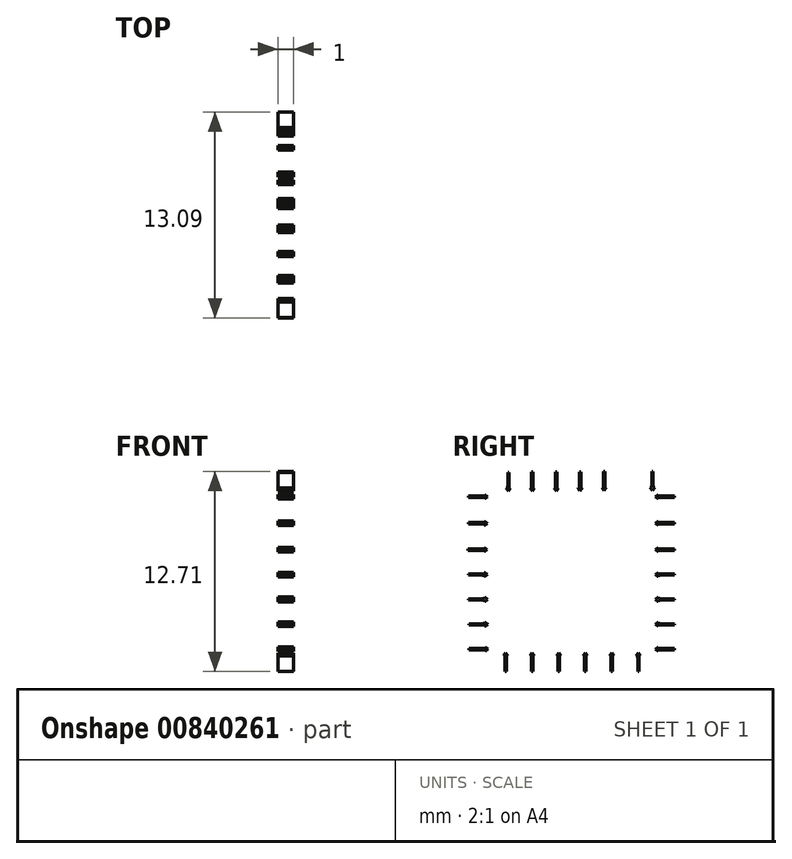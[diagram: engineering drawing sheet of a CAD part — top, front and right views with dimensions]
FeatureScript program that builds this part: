
annotation { "Feature Type Name" : "Feature", "Feature Type Description" : "" }
export const myFeature = defineFeature(function(context is Context, id is Id, definition is map)
    precondition{}
    {
        {
            var Q0;
            Q0=qCreatedBy(makeId("Right.planeOp"),FACE);
            var sketch = newSketch(context, id + "F0", { "sketchPlane" : qUnion([Q0])});
            skLineSegment(sketch, "E0.2.0", {"start": v(11.3, -4.37) * mm, "end": v(12.3, -4.37) * mm});
            skLineSegment(sketch, "E0.2.1", {"start": v(11.3, -4.55) * mm, "end": v(11.1, -4.4) * mm});
            skLineSegment(sketch, "E0.2.2", {"start": v(11.3, -4.44) * mm, "end": v(12.3, -4.44) * mm});
            skLineSegment(sketch, "E0.2.4", {"start": v(11.3, -4.26) * mm, "end": v(11.1, -4.4) * mm});
            skLineSegment(sketch, "E0.2.5", {"start": v(11.3, -4.44) * mm, "end": v(11.3, -4.55) * mm});
            skLineSegment(sketch, "E0.2.6", {"start": v(12.3, -4.44) * mm, "end": v(12.3, -4.37) * mm});
            skLineSegment(sketch, "E0.2.7", {"start": v(11.3, -4.37) * mm, "end": v(11.3, -4.26) * mm});
            skLineSegment(sketch, "E0.2.8", {"start": v(11.3, -4.44) * mm, "end": v(11.3, -4.37) * mm});
            skLineSegment(sketch, "E1.3.6.0", {"start": v(0.22, -4.26) * mm, "end": v(0.42, -4.4) * mm});
            skLineSegment(sketch, "E1.6.6.0", {"start": v(0.22, -4.37) * mm, "end": v(-0.78, -4.37) * mm});
            skLineSegment(sketch, "E1.8.6.0", {"start": v(0.22, -4.44) * mm, "end": v(-0.78, -4.44) * mm});
            skLineSegment(sketch, "E1.10.6.0", {"start": v(0.22, -4.55) * mm, "end": v(0.42, -4.4) * mm});
            skLineSegment(sketch, "E1.13.6.0", {"start": v(0.22, -4.37) * mm, "end": v(0.22, -4.26) * mm});
            skLineSegment(sketch, "E1.16.6.0", {"start": v(-0.78, -4.37) * mm, "end": v(-0.78, -4.44) * mm});
            skLineSegment(sketch, "E1.19.6.0", {"start": v(0.22, -4.44) * mm, "end": v(0.22, -4.55) * mm});
            skLineSegment(sketch, "E1.22.6.0", {"start": v(0.22, -4.37) * mm, "end": v(0.22, -4.44) * mm});
            skLineSegment(sketch, "E2.0.1.0", {"start": v(0.23, -2.76) * mm, "end": v(0.23, -2.87) * mm});
            skLineSegment(sketch, "E2.0.1.1", {"start": v(0.23, -2.58) * mm, "end": v(0.43, -2.72) * mm});
            skLineSegment(sketch, "E2.0.1.2", {"start": v(-0.77, -2.69) * mm, "end": v(-0.77, -2.76) * mm});
            skLineSegment(sketch, "E2.0.1.3", {"start": v(0.23, -2.87) * mm, "end": v(0.43, -2.72) * mm});
            skLineSegment(sketch, "E2.0.1.4", {"start": v(0.23, -2.69) * mm, "end": v(0.23, -2.58) * mm});
            skLineSegment(sketch, "E2.0.1.5", {"start": v(0.23, -2.69) * mm, "end": v(-0.77, -2.69) * mm});
            skLineSegment(sketch, "E2.0.1.6", {"start": v(0.23, -2.69) * mm, "end": v(0.23, -2.76) * mm});
            skLineSegment(sketch, "E2.0.1.7", {"start": v(0.23, -2.76) * mm, "end": v(-0.77, -2.76) * mm});
            skLineSegment(sketch, "E2.0.2.0", {"start": v(0.25, -1.08) * mm, "end": v(0.25, -1.2) * mm});
            skLineSegment(sketch, "E2.0.2.1", {"start": v(0.25, -0.9) * mm, "end": v(0.45, -1.04) * mm});
            skLineSegment(sketch, "E2.0.2.2", {"start": v(-0.76, -1) * mm, "end": v(-0.76, -1.08) * mm});
            skLineSegment(sketch, "E2.0.2.3", {"start": v(0.25, -1.2) * mm, "end": v(0.45, -1.04) * mm});
            skLineSegment(sketch, "E2.0.2.4", {"start": v(0.25, -1) * mm, "end": v(0.25, -0.9) * mm});
            skLineSegment(sketch, "E2.0.2.5", {"start": v(0.25, -1) * mm, "end": v(-0.76, -1) * mm});
            skLineSegment(sketch, "E2.0.2.6", {"start": v(0.25, -1) * mm, "end": v(0.25, -1.08) * mm});
            skLineSegment(sketch, "E2.0.2.7", {"start": v(0.25, -1.08) * mm, "end": v(-0.76, -1.08) * mm});
            skLineSegment(sketch, "E2.direction2", {"start": v(-0.78, -4.44) * mm, "end": v(-0.77, -2.76) * mm, "construction": true});
            skLineSegment(sketch, "E3.0.1.0", {"start": v(0.23, -6.13) * mm, "end": v(0.43, -5.98) * mm});
            skLineSegment(sketch, "E3.0.1.1", {"start": v(0.23, -6.02) * mm, "end": v(-0.77, -6.02) * mm});
            skLineSegment(sketch, "E3.0.1.2", {"start": v(0.23, -5.95) * mm, "end": v(-0.77, -5.95) * mm});
            skLineSegment(sketch, "E3.0.1.3", {"start": v(0.23, -6.02) * mm, "end": v(0.23, -6.13) * mm});
            skLineSegment(sketch, "E3.0.1.4", {"start": v(0.23, -5.84) * mm, "end": v(0.43, -5.98) * mm});
            skLineSegment(sketch, "E3.0.1.5", {"start": v(0.23, -5.95) * mm, "end": v(0.23, -5.84) * mm});
            skLineSegment(sketch, "E3.0.1.6", {"start": v(-0.77, -5.95) * mm, "end": v(-0.77, -6.02) * mm});
            skLineSegment(sketch, "E3.0.1.7", {"start": v(0.23, -5.95) * mm, "end": v(0.23, -6.02) * mm});
            skLineSegment(sketch, "E3.0.2.0", {"start": v(0.25, -7.71) * mm, "end": v(0.45, -7.56) * mm});
            skLineSegment(sketch, "E3.0.2.1", {"start": v(0.25, -7.6) * mm, "end": v(-0.76, -7.6) * mm});
            skLineSegment(sketch, "E3.0.2.2", {"start": v(0.25, -7.53) * mm, "end": v(-0.76, -7.53) * mm});
            skLineSegment(sketch, "E3.0.2.3", {"start": v(0.25, -7.6) * mm, "end": v(0.25, -7.71) * mm});
            skLineSegment(sketch, "E3.0.2.4", {"start": v(0.25, -7.42) * mm, "end": v(0.45, -7.56) * mm});
            skLineSegment(sketch, "E3.0.2.5", {"start": v(0.25, -7.53) * mm, "end": v(0.25, -7.42) * mm});
            skLineSegment(sketch, "E3.0.2.6", {"start": v(-0.76, -7.53) * mm, "end": v(-0.76, -7.6) * mm});
            skLineSegment(sketch, "E3.0.2.7", {"start": v(0.25, -7.53) * mm, "end": v(0.25, -7.6) * mm});
            skLineSegment(sketch, "E3.0.3.0", {"start": v(0.26, -9.29) * mm, "end": v(0.46, -9.14) * mm});
            skLineSegment(sketch, "E3.0.3.1", {"start": v(0.26, -9.18) * mm, "end": v(-0.75, -9.18) * mm});
            skLineSegment(sketch, "E3.0.3.2", {"start": v(0.26, -9.1) * mm, "end": v(-0.75, -9.1) * mm});
            skLineSegment(sketch, "E3.0.3.3", {"start": v(0.26, -9.18) * mm, "end": v(0.26, -9.29) * mm});
            skLineSegment(sketch, "E3.0.3.4", {"start": v(0.26, -9) * mm, "end": v(0.46, -9.14) * mm});
            skLineSegment(sketch, "E3.0.3.5", {"start": v(0.26, -9.1) * mm, "end": v(0.26, -9) * mm});
            skLineSegment(sketch, "E3.0.3.6", {"start": v(-0.75, -9.1) * mm, "end": v(-0.75, -9.18) * mm});
            skLineSegment(sketch, "E3.0.3.7", {"start": v(0.26, -9.1) * mm, "end": v(0.26, -9.18) * mm});
            skLineSegment(sketch, "E3.0.4.0", {"start": v(0.27, -10.87) * mm, "end": v(0.47, -10.72) * mm});
            skLineSegment(sketch, "E3.0.4.1", {"start": v(0.27, -10.76) * mm, "end": v(-0.73, -10.76) * mm});
            skLineSegment(sketch, "E3.0.4.2", {"start": v(0.27, -10.69) * mm, "end": v(-0.73, -10.69) * mm});
            skLineSegment(sketch, "E3.0.4.3", {"start": v(0.27, -10.76) * mm, "end": v(0.27, -10.87) * mm});
            skLineSegment(sketch, "E3.0.4.4", {"start": v(0.27, -10.57) * mm, "end": v(0.47, -10.72) * mm});
            skLineSegment(sketch, "E3.0.4.5", {"start": v(0.27, -10.69) * mm, "end": v(0.27, -10.57) * mm});
            skLineSegment(sketch, "E3.0.4.6", {"start": v(-0.73, -10.69) * mm, "end": v(-0.73, -10.76) * mm});
            skLineSegment(sketch, "E3.0.4.7", {"start": v(0.27, -10.69) * mm, "end": v(0.27, -10.76) * mm});
            skLineSegment(sketch, "E3.direction2", {"start": v(-0.78, -4.44) * mm, "end": v(-0.77, -6.02) * mm, "construction": true});
            skLineSegment(sketch, "E4.0.1.0", {"start": v(11.3, -2.58) * mm, "end": v(11.1, -2.72) * mm});
            skLineSegment(sketch, "E4.0.1.1", {"start": v(11.3, -2.76) * mm, "end": v(12.3, -2.76) * mm});
            skLineSegment(sketch, "E4.0.1.2", {"start": v(11.3, -2.87) * mm, "end": v(11.1, -2.72) * mm});
            skLineSegment(sketch, "E4.0.1.3", {"start": v(11.3, -2.69) * mm, "end": v(12.3, -2.69) * mm});
            skLineSegment(sketch, "E4.0.1.4", {"start": v(12.3, -2.76) * mm, "end": v(12.3, -2.69) * mm});
            skLineSegment(sketch, "E4.0.1.5", {"start": v(11.3, -2.76) * mm, "end": v(11.3, -2.87) * mm});
            skLineSegment(sketch, "E4.0.1.6", {"start": v(11.3, -2.69) * mm, "end": v(11.3, -2.58) * mm});
            skLineSegment(sketch, "E4.0.1.7", {"start": v(11.3, -2.76) * mm, "end": v(11.3, -2.69) * mm});
            skLineSegment(sketch, "E4.0.2.0", {"start": v(11.3, -0.9) * mm, "end": v(11.1, -1.04) * mm});
            skLineSegment(sketch, "E4.0.2.1", {"start": v(11.3, -1.08) * mm, "end": v(12.3, -1.08) * mm});
            skLineSegment(sketch, "E4.0.2.2", {"start": v(11.3, -1.19) * mm, "end": v(11.1, -1.04) * mm});
            skLineSegment(sketch, "E4.0.2.3", {"start": v(11.3, -1) * mm, "end": v(12.3, -1) * mm});
            skLineSegment(sketch, "E4.0.2.4", {"start": v(12.3, -1.08) * mm, "end": v(12.3, -1) * mm});
            skLineSegment(sketch, "E4.0.2.5", {"start": v(11.3, -1.08) * mm, "end": v(11.3, -1.19) * mm});
            skLineSegment(sketch, "E4.0.2.6", {"start": v(11.3, -1) * mm, "end": v(11.3, -0.9) * mm});
            skLineSegment(sketch, "E4.0.2.7", {"start": v(11.3, -1.08) * mm, "end": v(11.3, -1) * mm});
            skLineSegment(sketch, "E4.direction2", {"start": v(11.1, -4.4) * mm, "end": v(11.1, -2.72) * mm, "construction": true});
            skLineSegment(sketch, "E5.0", {"start": v(11.3, -5.95) * mm, "end": v(12.3, -5.95) * mm});
            skLineSegment(sketch, "E6.0.1.0", {"start": v(11.3, -6.02) * mm, "end": v(11.3, -5.95) * mm});
            skLineSegment(sketch, "E6.0.1.1", {"start": v(11.3, -6.02) * mm, "end": v(11.3, -6.13) * mm});
            skLineSegment(sketch, "E6.0.1.2", {"start": v(11.3, -6.02) * mm, "end": v(12.3, -6.02) * mm});
            skLineSegment(sketch, "E6.0.1.3", {"start": v(11.3, -5.84) * mm, "end": v(11.1, -5.98) * mm});
            skLineSegment(sketch, "E6.0.1.5", {"start": v(11.3, -5.95) * mm, "end": v(11.3, -5.84) * mm});
            skLineSegment(sketch, "E6.0.1.6", {"start": v(12.3, -6.02) * mm, "end": v(12.3, -5.95) * mm});
            skLineSegment(sketch, "E6.0.1.7", {"start": v(11.3, -6.13) * mm, "end": v(11.1, -5.98) * mm});
            skLineSegment(sketch, "E6.0.2.0", {"start": v(11.3, -7.6) * mm, "end": v(11.3, -7.53) * mm});
            skLineSegment(sketch, "E6.0.2.1", {"start": v(11.3, -7.6) * mm, "end": v(11.3, -7.71) * mm});
            skLineSegment(sketch, "E6.0.2.2", {"start": v(11.3, -7.6) * mm, "end": v(12.3, -7.6) * mm});
            skLineSegment(sketch, "E6.0.2.3", {"start": v(11.3, -7.42) * mm, "end": v(11.1, -7.56) * mm});
            skLineSegment(sketch, "E6.0.2.4", {"start": v(11.3, -7.53) * mm, "end": v(12.3, -7.53) * mm});
            skLineSegment(sketch, "E6.0.2.5", {"start": v(11.3, -7.53) * mm, "end": v(11.3, -7.42) * mm});
            skLineSegment(sketch, "E6.0.2.6", {"start": v(12.3, -7.6) * mm, "end": v(12.3, -7.53) * mm});
            skLineSegment(sketch, "E6.0.2.7", {"start": v(11.3, -7.71) * mm, "end": v(11.1, -7.56) * mm});
            skLineSegment(sketch, "E6.0.3.0", {"start": v(11.3, -9.18) * mm, "end": v(11.3, -9.1) * mm});
            skLineSegment(sketch, "E6.0.3.1", {"start": v(11.3, -9.18) * mm, "end": v(11.3, -9.3) * mm});
            skLineSegment(sketch, "E6.0.3.2", {"start": v(11.3, -9.18) * mm, "end": v(12.3, -9.18) * mm});
            skLineSegment(sketch, "E6.0.3.3", {"start": v(11.3, -9) * mm, "end": v(11.1, -9.14) * mm});
            skLineSegment(sketch, "E6.0.3.4", {"start": v(11.3, -9.1) * mm, "end": v(12.3, -9.1) * mm});
            skLineSegment(sketch, "E6.0.3.5", {"start": v(11.3, -9.1) * mm, "end": v(11.3, -9) * mm});
            skLineSegment(sketch, "E6.0.3.6", {"start": v(12.3, -9.18) * mm, "end": v(12.3, -9.1) * mm});
            skLineSegment(sketch, "E6.0.3.7", {"start": v(11.3, -9.3) * mm, "end": v(11.1, -9.14) * mm});
            skLineSegment(sketch, "E6.0.4.0", {"start": v(11.3, -10.76) * mm, "end": v(11.3, -10.69) * mm});
            skLineSegment(sketch, "E6.0.4.1", {"start": v(11.3, -10.76) * mm, "end": v(11.3, -10.87) * mm});
            skLineSegment(sketch, "E6.0.4.2", {"start": v(11.3, -10.76) * mm, "end": v(12.3, -10.76) * mm});
            skLineSegment(sketch, "E6.0.4.3", {"start": v(11.3, -10.58) * mm, "end": v(11.1, -10.72) * mm});
            skLineSegment(sketch, "E6.0.4.4", {"start": v(11.3, -10.69) * mm, "end": v(12.3, -10.69) * mm});
            skLineSegment(sketch, "E6.0.4.5", {"start": v(11.3, -10.69) * mm, "end": v(11.3, -10.58) * mm});
            skLineSegment(sketch, "E6.0.4.6", {"start": v(12.3, -10.76) * mm, "end": v(12.3, -10.69) * mm});
            skLineSegment(sketch, "E6.0.4.7", {"start": v(11.3, -10.87) * mm, "end": v(11.1, -10.72) * mm});
            skLineSegment(sketch, "E6.direction2", {"start": v(11.1, -4.4) * mm, "end": v(11.1, -5.98) * mm, "construction": true});
            skLineSegment(sketch, "E7", {"start": v(1.56, -11.15) * mm, "end": v(1.56, -12.15) * mm});
            skLineSegment(sketch, "E8", {"start": v(1.63, -11.15) * mm, "end": v(1.63, -12.15) * mm});
            skLineSegment(sketch, "E9", {"start": v(1.56, -12.15) * mm, "end": v(1.63, -12.15) * mm});
            skLineSegment(sketch, "E10", {"start": v(1.56, -11.15) * mm, "end": v(1.63, -11.15) * mm});
            skLineSegment(sketch, "E11", {"start": v(1.56, -11.15) * mm, "end": v(1.45, -11.15) * mm});
            skLineSegment(sketch, "E12", {"start": v(1.45, -11.15) * mm, "end": v(1.6, -10.95) * mm});
            skLineSegment(sketch, "E13", {"start": v(1.63, -11.15) * mm, "end": v(1.75, -11.15) * mm});
            skLineSegment(sketch, "E14", {"start": v(1.75, -11.15) * mm, "end": v(1.6, -10.95) * mm});
            skLineSegment(sketch, "E15.1.0.0", {"start": v(3.25, -11.15) * mm, "end": v(3.25, -12.15) * mm});
            skLineSegment(sketch, "E15.1.0.1", {"start": v(3.32, -11.15) * mm, "end": v(3.32, -12.15) * mm});
            skLineSegment(sketch, "E15.1.0.2", {"start": v(3.25, -12.15) * mm, "end": v(3.32, -12.15) * mm});
            skLineSegment(sketch, "E15.1.0.3", {"start": v(3.25, -11.15) * mm, "end": v(3.14, -11.15) * mm});
            skLineSegment(sketch, "E15.1.0.4", {"start": v(3.14, -11.15) * mm, "end": v(3.28, -10.95) * mm});
            skLineSegment(sketch, "E15.1.0.5", {"start": v(3.43, -11.15) * mm, "end": v(3.28, -10.95) * mm});
            skLineSegment(sketch, "E15.1.0.6", {"start": v(3.32, -11.15) * mm, "end": v(3.43, -11.15) * mm});
            skLineSegment(sketch, "E15.1.0.7", {"start": v(3.25, -11.15) * mm, "end": v(3.32, -11.15) * mm});
            skLineSegment(sketch, "E15.2.0.0", {"start": v(4.93, -11.15) * mm, "end": v(4.93, -12.15) * mm});
            skLineSegment(sketch, "E15.2.0.1", {"start": v(5, -11.15) * mm, "end": v(5, -12.15) * mm});
            skLineSegment(sketch, "E15.2.0.2", {"start": v(4.93, -12.15) * mm, "end": v(5, -12.15) * mm});
            skLineSegment(sketch, "E15.2.0.3", {"start": v(4.93, -11.15) * mm, "end": v(4.82, -11.15) * mm});
            skLineSegment(sketch, "E15.2.0.4", {"start": v(4.82, -11.15) * mm, "end": v(4.97, -10.95) * mm});
            skLineSegment(sketch, "E15.2.0.5", {"start": v(5.11, -11.15) * mm, "end": v(4.97, -10.95) * mm});
            skLineSegment(sketch, "E15.2.0.6", {"start": v(5, -11.15) * mm, "end": v(5.11, -11.15) * mm});
            skLineSegment(sketch, "E15.2.0.7", {"start": v(4.93, -11.15) * mm, "end": v(5, -11.15) * mm});
            skLineSegment(sketch, "E15.3.0.0", {"start": v(6.62, -11.15) * mm, "end": v(6.62, -12.15) * mm});
            skLineSegment(sketch, "E15.3.0.1", {"start": v(6.69, -11.15) * mm, "end": v(6.69, -12.15) * mm});
            skLineSegment(sketch, "E15.3.0.2", {"start": v(6.62, -12.15) * mm, "end": v(6.69, -12.15) * mm});
            skLineSegment(sketch, "E15.3.0.3", {"start": v(6.62, -11.15) * mm, "end": v(6.5, -11.15) * mm});
            skLineSegment(sketch, "E15.3.0.4", {"start": v(6.5, -11.15) * mm, "end": v(6.65, -10.95) * mm});
            skLineSegment(sketch, "E15.3.0.5", {"start": v(6.8, -11.15) * mm, "end": v(6.65, -10.95) * mm});
            skLineSegment(sketch, "E15.3.0.6", {"start": v(6.69, -11.15) * mm, "end": v(6.8, -11.15) * mm});
            skLineSegment(sketch, "E15.3.0.7", {"start": v(6.62, -11.15) * mm, "end": v(6.69, -11.15) * mm});
            skLineSegment(sketch, "E15.4.0.0", {"start": v(8.3, -11.15) * mm, "end": v(8.3, -12.15) * mm});
            skLineSegment(sketch, "E15.4.0.1", {"start": v(8.37, -11.15) * mm, "end": v(8.37, -12.15) * mm});
            skLineSegment(sketch, "E15.4.0.2", {"start": v(8.3, -12.15) * mm, "end": v(8.37, -12.15) * mm});
            skLineSegment(sketch, "E15.4.0.3", {"start": v(8.3, -11.15) * mm, "end": v(8.19, -11.15) * mm});
            skLineSegment(sketch, "E15.4.0.4", {"start": v(8.19, -11.15) * mm, "end": v(8.34, -10.95) * mm});
            skLineSegment(sketch, "E15.4.0.5", {"start": v(8.48, -11.15) * mm, "end": v(8.34, -10.95) * mm});
            skLineSegment(sketch, "E15.4.0.6", {"start": v(8.37, -11.15) * mm, "end": v(8.48, -11.15) * mm});
            skLineSegment(sketch, "E15.4.0.7", {"start": v(8.3, -11.15) * mm, "end": v(8.37, -11.15) * mm});
            skLineSegment(sketch, "E15.5.0.0", {"start": v(9.98, -11.15) * mm, "end": v(9.98, -12.15) * mm});
            skLineSegment(sketch, "E15.5.0.1", {"start": v(10.06, -11.15) * mm, "end": v(10.06, -12.15) * mm});
            skLineSegment(sketch, "E15.5.0.2", {"start": v(9.98, -12.15) * mm, "end": v(10.06, -12.15) * mm});
            skLineSegment(sketch, "E15.5.0.3", {"start": v(9.98, -11.15) * mm, "end": v(9.87, -11.15) * mm});
            skLineSegment(sketch, "E15.5.0.4", {"start": v(9.87, -11.15) * mm, "end": v(10.02, -10.95) * mm});
            skLineSegment(sketch, "E15.5.0.5", {"start": v(10.17, -11.15) * mm, "end": v(10.02, -10.95) * mm});
            skLineSegment(sketch, "E15.5.0.6", {"start": v(10.06, -11.15) * mm, "end": v(10.17, -11.15) * mm});
            skLineSegment(sketch, "E15.5.0.7", {"start": v(9.98, -11.15) * mm, "end": v(10.06, -11.15) * mm});
            skLineSegment(sketch, "E15.direction1", {"start": v(1.56, -12.15) * mm, "end": v(3.25, -12.15) * mm, "construction": true});
            skLineSegment(sketch, "E16.4.0", {"start": v(1.73, -0.49) * mm, "end": v(1.73, 0.52) * mm});
            skLineSegment(sketch, "E16.4.1", {"start": v(1.92, -0.49) * mm, "end": v(1.77, -0.69) * mm});
            skLineSegment(sketch, "E16.4.2", {"start": v(1.8, -0.49) * mm, "end": v(1.8, 0.52) * mm});
            skLineSegment(sketch, "E16.4.4", {"start": v(1.62, -0.49) * mm, "end": v(1.77, -0.69) * mm});
            skLineSegment(sketch, "E16.4.5", {"start": v(1.8, -0.49) * mm, "end": v(1.92, -0.49) * mm});
            skLineSegment(sketch, "E16.4.6", {"start": v(1.8, 0.52) * mm, "end": v(1.73, 0.52) * mm});
            skLineSegment(sketch, "E16.4.8", {"start": v(1.8, -0.49) * mm, "end": v(1.73, -0.49) * mm});
            skLineSegment(sketch, "E17.1.0.0", {"start": v(3.33, -0.48) * mm, "end": v(3.33, 0.52) * mm});
            skLineSegment(sketch, "E17.1.0.1", {"start": v(3.25, -0.48) * mm, "end": v(3.25, 0.52) * mm});
            skLineSegment(sketch, "E17.1.0.2", {"start": v(3.14, -0.48) * mm, "end": v(3.29, -0.68) * mm});
            skLineSegment(sketch, "E17.1.0.3", {"start": v(3.33, 0.52) * mm, "end": v(3.25, 0.52) * mm});
            skLineSegment(sketch, "E17.1.0.4", {"start": v(3.44, -0.48) * mm, "end": v(3.29, -0.68) * mm});
            skLineSegment(sketch, "E17.1.0.5", {"start": v(3.33, -0.48) * mm, "end": v(3.25, -0.48) * mm});
            skLineSegment(sketch, "E17.1.0.6", {"start": v(3.33, -0.48) * mm, "end": v(3.44, -0.48) * mm});
            skLineSegment(sketch, "E17.2.0.0", {"start": v(4.85, -0.47) * mm, "end": v(4.85, 0.53) * mm});
            skLineSegment(sketch, "E17.2.0.1", {"start": v(4.77, -0.47) * mm, "end": v(4.77, 0.53) * mm});
            skLineSegment(sketch, "E17.2.0.2", {"start": v(4.66, -0.47) * mm, "end": v(4.81, -0.67) * mm});
            skLineSegment(sketch, "E17.2.0.3", {"start": v(4.85, 0.53) * mm, "end": v(4.77, 0.53) * mm});
            skLineSegment(sketch, "E17.2.0.4", {"start": v(4.96, -0.47) * mm, "end": v(4.81, -0.67) * mm});
            skLineSegment(sketch, "E17.2.0.5", {"start": v(4.85, -0.47) * mm, "end": v(4.77, -0.47) * mm});
            skLineSegment(sketch, "E17.2.0.6", {"start": v(4.85, -0.47) * mm, "end": v(4.96, -0.47) * mm});
            skLineSegment(sketch, "E17.3.0.0", {"start": v(6.37, -0.46) * mm, "end": v(6.37, 0.54) * mm});
            skLineSegment(sketch, "E17.3.0.1", {"start": v(6.3, -0.46) * mm, "end": v(6.3, 0.54) * mm});
            skLineSegment(sketch, "E17.3.0.2", {"start": v(6.18, -0.46) * mm, "end": v(6.33, -0.66) * mm});
            skLineSegment(sketch, "E17.3.0.3", {"start": v(6.37, 0.54) * mm, "end": v(6.3, 0.54) * mm});
            skLineSegment(sketch, "E17.3.0.4", {"start": v(6.48, -0.46) * mm, "end": v(6.33, -0.66) * mm});
            skLineSegment(sketch, "E17.3.0.5", {"start": v(6.37, -0.46) * mm, "end": v(6.3, -0.46) * mm});
            skLineSegment(sketch, "E17.3.0.6", {"start": v(6.37, -0.46) * mm, "end": v(6.48, -0.46) * mm});
            skLineSegment(sketch, "E17.4.0.0", {"start": v(7.89, -0.45) * mm, "end": v(7.89, 0.55) * mm});
            skLineSegment(sketch, "E17.4.0.1", {"start": v(7.81, -0.45) * mm, "end": v(7.81, 0.55) * mm});
            skLineSegment(sketch, "E17.4.0.2", {"start": v(7.7, -0.45) * mm, "end": v(7.85, -0.65) * mm});
            skLineSegment(sketch, "E17.4.0.3", {"start": v(7.89, 0.55) * mm, "end": v(7.81, 0.55) * mm});
            skLineSegment(sketch, "E17.4.0.4", {"start": v(8, -0.45) * mm, "end": v(7.85, -0.65) * mm});
            skLineSegment(sketch, "E17.4.0.5", {"start": v(7.89, -0.45) * mm, "end": v(7.81, -0.45) * mm});
            skLineSegment(sketch, "E17.4.0.6", {"start": v(7.89, -0.45) * mm, "end": v(8, -0.45) * mm});
            skLineSegment(sketch, "E17.5.0.0", {"start": v(10.96, -0.44) * mm, "end": v(10.96, 0.56) * mm});
            skLineSegment(sketch, "E17.5.0.1", {"start": v(10.89, -0.44) * mm, "end": v(10.89, 0.56) * mm});
            skLineSegment(sketch, "E17.5.0.2", {"start": v(10.78, -0.44) * mm, "end": v(10.92, -0.64) * mm});
            skLineSegment(sketch, "E17.5.0.3", {"start": v(10.96, 0.56) * mm, "end": v(10.89, 0.56) * mm});
            skLineSegment(sketch, "E17.5.0.4", {"start": v(11.07, -0.44) * mm, "end": v(10.92, -0.64) * mm});
            skLineSegment(sketch, "E17.5.0.5", {"start": v(10.96, -0.44) * mm, "end": v(10.89, -0.44) * mm});
            skLineSegment(sketch, "E17.5.0.6", {"start": v(10.96, -0.44) * mm, "end": v(11.07, -0.44) * mm});
            skLineSegment(sketch, "E17.direction1", {"start": v(1.77, -0.69) * mm, "end": v(3.29, -0.68) * mm, "construction": true});
            skLineSegment(sketch, "E18", {"start": v(1.73, -0.49) * mm, "end": v(1.62, -0.49) * mm});
            skLineSegment(sketch, "E19", {"start": v(3.14, -0.48) * mm, "end": v(3.25, -0.48) * mm});
            skLineSegment(sketch, "E20", {"start": v(4.77, -0.47) * mm, "end": v(4.66, -0.47) * mm});
            skLineSegment(sketch, "E21", {"start": v(6.3, -0.46) * mm, "end": v(6.18, -0.46) * mm});
            skLineSegment(sketch, "E22", {"start": v(7.81, -0.45) * mm, "end": v(7.7, -0.45) * mm});
            skLineSegment(sketch, "E23", {"start": v(10.89, -0.44) * mm, "end": v(10.78, -0.44) * mm});
            skSolve(sketch);
        }
        {
            var Q0;
            Q0=makeQuery(id+"F0.imprint","IMPRINT",FACE,{"disambiguationData":[TD([[makeQuery(id+"F0.imprint","IMPRINT",EDGE,{"derivedFrom":sQuery(id+"F0.wireOp",EDGE,"E4.0.1.1")}),1.0]])]});
            var Q1;
            Q1=makeQuery(id+"F0.imprint","IMPRINT",FACE,{"disambiguationData":[TD([[makeQuery(id+"F0.imprint","IMPRINT",EDGE,{"derivedFrom":sQuery(id+"F0.wireOp",EDGE,"E0.2.0")}),-1.0]])]});
            var Q2;
            Q2=makeQuery(id+"F0.imprint","IMPRINT",FACE,{"disambiguationData":[TD([[makeQuery(id+"F0.imprint","IMPRINT",EDGE,{"derivedFrom":sQuery(id+"F0.wireOp",EDGE,"E3.0.3.1")}),-1.0]])]});
            var Q3;
            Q3=makeQuery(id+"F0.imprint","IMPRINT",FACE,{"disambiguationData":[TD([[makeQuery(id+"F0.imprint","IMPRINT",EDGE,{"derivedFrom":sQuery(id+"F0.wireOp",EDGE,"E6.0.2.0")}),-1.0]])]});
            var Q4;
            Q4=makeQuery(id+"F0.imprint","IMPRINT",FACE,{"disambiguationData":[TD([[makeQuery(id+"F0.imprint","IMPRINT",EDGE,{"derivedFrom":sQuery(id+"F0.wireOp",EDGE,"E6.0.3.0")}),-1.0]])]});
            var Q5;
            Q5=makeQuery(id+"F0.imprint","IMPRINT",FACE,{"disambiguationData":[TD([[makeQuery(id+"F0.imprint","IMPRINT",EDGE,{"derivedFrom":sQuery(id+"F0.wireOp",EDGE,"E6.0.4.0")}),-1.0]])]});
            var Q6;
            Q6=makeQuery(id+"F0.imprint","IMPRINT",FACE,{"disambiguationData":[TD([[makeQuery(id+"F0.imprint","IMPRINT",EDGE,{"derivedFrom":sQuery(id+"F0.wireOp",EDGE,"E4.0.2.1")}),1.0]])]});
            var Q7;
            Q7=makeQuery(id+"F0.imprint","IMPRINT",FACE,{"disambiguationData":[TD([[makeQuery(id+"F0.imprint","IMPRINT",EDGE,{"derivedFrom":sQuery(id+"F0.wireOp",EDGE,"E3.0.4.1")}),-1.0]])]});
            var Q8;
            Q8=makeQuery(id+"F0.imprint","IMPRINT",FACE,{"disambiguationData":[TD([[makeQuery(id+"F0.imprint","IMPRINT",EDGE,{"derivedFrom":sQuery(id+"F0.wireOp",EDGE,"E6.0.1.0")}),-1.0]])]});
            var Q9;
            Q9=makeQuery(id+"F0.imprint","IMPRINT",FACE,{"disambiguationData":[TD([[makeQuery(id+"F0.imprint","IMPRINT",EDGE,{"derivedFrom":sQuery(id+"F0.wireOp",EDGE,"E17.2.0.0")}),1.0]])]});
            var Q10;
            Q10=makeQuery(id+"F0.imprint","IMPRINT",FACE,{"disambiguationData":[TD([[makeQuery(id+"F0.imprint","IMPRINT",EDGE,{"derivedFrom":sQuery(id+"F0.wireOp",EDGE,"E17.5.0.0")}),1.0]])]});
            var Q11;
            Q11=makeQuery(id+"F0.imprint","IMPRINT",FACE,{"disambiguationData":[TD([[makeQuery(id+"F0.imprint","IMPRINT",EDGE,{"derivedFrom":sQuery(id+"F0.wireOp",EDGE,"E15.5.0.0")}),1.0]])]});
            var Q12;
            Q12=makeQuery(id+"F0.imprint","IMPRINT",FACE,{"disambiguationData":[TD([[makeQuery(id+"F0.imprint","IMPRINT",EDGE,{"derivedFrom":sQuery(id+"F0.wireOp",EDGE,"E3.0.1.1")}),-1.0]])]});
            var Q13;
            Q13=makeQuery(id+"F0.imprint","IMPRINT",FACE,{"disambiguationData":[TD([[makeQuery(id+"F0.imprint","IMPRINT",EDGE,{"derivedFrom":sQuery(id+"F0.wireOp",EDGE,"E15.4.0.0")}),1.0]])]});
            var Q14;
            Q14=makeQuery(id+"F0.imprint","IMPRINT",FACE,{"disambiguationData":[TD([[makeQuery(id+"F0.imprint","IMPRINT",EDGE,{"derivedFrom":sQuery(id+"F0.wireOp",EDGE,"E17.1.0.0")}),1.0]])]});
            var Q15;
            Q15=makeQuery(id+"F0.imprint","IMPRINT",FACE,{"disambiguationData":[TD([[makeQuery(id+"F0.imprint","IMPRINT",EDGE,{"derivedFrom":sQuery(id+"F0.wireOp",EDGE,"E7")}),1.0]])]});
            var Q16;
            Q16=makeQuery(id+"F0.imprint","IMPRINT",FACE,{"disambiguationData":[TD([[makeQuery(id+"F0.imprint","IMPRINT",EDGE,{"derivedFrom":sQuery(id+"F0.wireOp",EDGE,"E17.4.0.0")}),1.0]])]});
            var Q17;
            Q17=makeQuery(id+"F0.imprint","IMPRINT",FACE,{"disambiguationData":[TD([[makeQuery(id+"F0.imprint","IMPRINT",EDGE,{"derivedFrom":sQuery(id+"F0.wireOp",EDGE,"E16.4.0")}),-1.0]])]});
            var Q18;
            Q18=makeQuery(id+"F0.imprint","IMPRINT",FACE,{"disambiguationData":[TD([[makeQuery(id+"F0.imprint","IMPRINT",EDGE,{"derivedFrom":sQuery(id+"F0.wireOp",EDGE,"E2.0.2.2")}),1.0]])]});
            var Q19;
            Q19=makeQuery(id+"F0.imprint","IMPRINT",FACE,{"disambiguationData":[TD([[makeQuery(id+"F0.imprint","IMPRINT",EDGE,{"derivedFrom":sQuery(id+"F0.wireOp",EDGE,"E17.3.0.0")}),1.0]])]});
            var Q20;
            Q20=makeQuery(id+"F0.imprint","IMPRINT",FACE,{"disambiguationData":[TD([[makeQuery(id+"F0.imprint","IMPRINT",EDGE,{"derivedFrom":sQuery(id+"F0.wireOp",EDGE,"E15.3.0.0")}),1.0]])]});
            var Q21;
            Q21=makeQuery(id+"F0.imprint","IMPRINT",FACE,{"disambiguationData":[TD([[makeQuery(id+"F0.imprint","IMPRINT",EDGE,{"derivedFrom":sQuery(id+"F0.wireOp",EDGE,"E17.2.0.2")}),1.0]])]});
            var Q22;
            Q22=makeQuery(id+"F0.imprint","IMPRINT",FACE,{"disambiguationData":[TD([[makeQuery(id+"F0.imprint","IMPRINT",EDGE,{"derivedFrom":sQuery(id+"F0.wireOp",EDGE,"E15.2.0.0")}),1.0]])]});
            var Q23;
            Q23=makeQuery(id+"F0.imprint","IMPRINT",FACE,{"disambiguationData":[TD([[makeQuery(id+"F0.imprint","IMPRINT",EDGE,{"derivedFrom":sQuery(id+"F0.wireOp",EDGE,"E3.0.1.0")}),1.0]])]});
            var Q24;
            Q24=makeQuery(id+"F0.imprint","IMPRINT",FACE,{"disambiguationData":[TD([[makeQuery(id+"F0.imprint","IMPRINT",EDGE,{"derivedFrom":sQuery(id+"F0.wireOp",EDGE,"E0.2.1")}),-1.0]])]});
            var Q25;
            Q25=makeQuery(id+"F0.imprint","IMPRINT",FACE,{"disambiguationData":[TD([[makeQuery(id+"F0.imprint","IMPRINT",EDGE,{"derivedFrom":sQuery(id+"F0.wireOp",EDGE,"E10")}),1.0]])]});
            var Q26;
            Q26=makeQuery(id+"F0.imprint","IMPRINT",FACE,{"disambiguationData":[TD([[makeQuery(id+"F0.imprint","IMPRINT",EDGE,{"derivedFrom":sQuery(id+"F0.wireOp",EDGE,"E2.0.1.2")}),1.0]])]});
            var Q27;
            Q27=makeQuery(id+"F0.imprint","IMPRINT",FACE,{"disambiguationData":[TD([[makeQuery(id+"F0.imprint","IMPRINT",EDGE,{"derivedFrom":sQuery(id+"F0.wireOp",EDGE,"E3.0.2.1")}),-1.0]])]});
            var Q28;
            Q28=makeQuery(id+"F0.imprint","IMPRINT",FACE,{"disambiguationData":[TD([[makeQuery(id+"F0.imprint","IMPRINT",EDGE,{"derivedFrom":sQuery(id+"F0.wireOp",EDGE,"E15.1.0.0")}),1.0]])]});
            var Q29;
            Q29=makeQuery(id+"F0.imprint","IMPRINT",FACE,{"disambiguationData":[TD([[makeQuery(id+"F0.imprint","IMPRINT",EDGE,{"derivedFrom":sQuery(id+"F0.wireOp",EDGE,"E1.6.6.0")}),1.0]])]});
            var Q30;
            Q30=makeQuery(id+"F0.imprint","IMPRINT",FACE,{"disambiguationData":[TD([[makeQuery(id+"F0.imprint","IMPRINT",EDGE,{"derivedFrom":sQuery(id+"F0.wireOp",EDGE,"E4.0.1.0")}),1.0]])]});
            var Q31;
            Q31=makeQuery(id+"F0.imprint","IMPRINT",FACE,{"disambiguationData":[TD([[makeQuery(id+"F0.imprint","IMPRINT",EDGE,{"derivedFrom":sQuery(id+"F0.wireOp",EDGE,"E1.3.6.0")}),-1.0]])]});
            var Q32;
            Q32=makeQuery(id+"F0.imprint","IMPRINT",FACE,{"disambiguationData":[TD([[makeQuery(id+"F0.imprint","IMPRINT",EDGE,{"derivedFrom":sQuery(id+"F0.wireOp",EDGE,"E17.1.0.2")}),1.0]])]});
            var Q33;
            Q33=makeQuery(id+"F0.imprint","IMPRINT",FACE,{"disambiguationData":[TD([[makeQuery(id+"F0.imprint","IMPRINT",EDGE,{"derivedFrom":sQuery(id+"F0.wireOp",EDGE,"E17.5.0.2")}),1.0]])]});
            var Q34;
            Q34=makeQuery(id+"F0.imprint","IMPRINT",FACE,{"disambiguationData":[TD([[makeQuery(id+"F0.imprint","IMPRINT",EDGE,{"derivedFrom":sQuery(id+"F0.wireOp",EDGE,"E15.4.0.3")}),-1.0]])]});
            var Q35;
            Q35=makeQuery(id+"F0.imprint","IMPRINT",FACE,{"disambiguationData":[TD([[makeQuery(id+"F0.imprint","IMPRINT",EDGE,{"derivedFrom":sQuery(id+"F0.wireOp",EDGE,"E15.5.0.3")}),-1.0]])]});
            var Q36;
            Q36=makeQuery(id+"F0.imprint","IMPRINT",FACE,{"disambiguationData":[TD([[makeQuery(id+"F0.imprint","IMPRINT",EDGE,{"derivedFrom":sQuery(id+"F0.wireOp",EDGE,"E15.1.0.3")}),-1.0]])]});
            var Q37;
            Q37=makeQuery(id+"F0.imprint","IMPRINT",FACE,{"disambiguationData":[TD([[makeQuery(id+"F0.imprint","IMPRINT",EDGE,{"derivedFrom":sQuery(id+"F0.wireOp",EDGE,"E2.0.1.0")}),1.0]])]});
            var Q38;
            Q38=makeQuery(id+"F0.imprint","IMPRINT",FACE,{"disambiguationData":[TD([[makeQuery(id+"F0.imprint","IMPRINT",EDGE,{"derivedFrom":sQuery(id+"F0.wireOp",EDGE,"E17.4.0.2")}),1.0]])]});
            var Q39;
            {var subQ3=sQuery(id+"F0.wireOp",EDGE,"E6.0.1.0");Q39=makeQuery(id+"F0.imprint","IMPRINT",FACE,{"disambiguationData":[TD([[makeQuery(id+"F0.imprint","IMPRINT",EDGE,{"derivedFrom":subQ3}),1.0]])]});}
            var Q40;
            Q40=makeQuery(id+"F0.imprint","IMPRINT",FACE,{"disambiguationData":[TD([[makeQuery(id+"F0.imprint","IMPRINT",EDGE,{"derivedFrom":sQuery(id+"F0.wireOp",EDGE,"E3.0.2.0")}),1.0]])]});
            var Q41;
            Q41=makeQuery(id+"F0.imprint","IMPRINT",FACE,{"disambiguationData":[TD([[makeQuery(id+"F0.imprint","IMPRINT",EDGE,{"derivedFrom":sQuery(id+"F0.wireOp",EDGE,"E2.0.2.0")}),1.0]])]});
            var Q42;
            Q42=makeQuery(id+"F0.imprint","IMPRINT",FACE,{"disambiguationData":[TD([[makeQuery(id+"F0.imprint","IMPRINT",EDGE,{"derivedFrom":sQuery(id+"F0.wireOp",EDGE,"E15.3.0.3")}),-1.0]])]});
            var Q43;
            Q43=makeQuery(id+"F0.imprint","IMPRINT",FACE,{"disambiguationData":[TD([[makeQuery(id+"F0.imprint","IMPRINT",EDGE,{"derivedFrom":sQuery(id+"F0.wireOp",EDGE,"E15.2.0.3")}),-1.0]])]});
            var Q44;
            Q44=makeQuery(id+"F0.imprint","IMPRINT",FACE,{"disambiguationData":[TD([[makeQuery(id+"F0.imprint","IMPRINT",EDGE,{"derivedFrom":sQuery(id+"F0.wireOp",EDGE,"E6.0.2.0")}),1.0]])]});
            var Q45;
            Q45=makeQuery(id+"F0.imprint","IMPRINT",FACE,{"disambiguationData":[TD([[makeQuery(id+"F0.imprint","IMPRINT",EDGE,{"derivedFrom":sQuery(id+"F0.wireOp",EDGE,"E6.0.4.0")}),1.0]])]});
            var Q46;
            Q46=makeQuery(id+"F0.imprint","IMPRINT",FACE,{"disambiguationData":[TD([[makeQuery(id+"F0.imprint","IMPRINT",EDGE,{"derivedFrom":sQuery(id+"F0.wireOp",EDGE,"E17.3.0.2")}),1.0]])]});
            var Q47;
            Q47=makeQuery(id+"F0.imprint","IMPRINT",FACE,{"disambiguationData":[TD([[makeQuery(id+"F0.imprint","IMPRINT",EDGE,{"derivedFrom":sQuery(id+"F0.wireOp",EDGE,"E16.4.1")}),-1.0]])]});
            var Q48;
            Q48=makeQuery(id+"F0.imprint","IMPRINT",FACE,{"disambiguationData":[TD([[makeQuery(id+"F0.imprint","IMPRINT",EDGE,{"derivedFrom":sQuery(id+"F0.wireOp",EDGE,"E6.0.3.0")}),1.0]])]});
            var Q49;
            Q49=makeQuery(id+"F0.imprint","IMPRINT",FACE,{"disambiguationData":[TD([[makeQuery(id+"F0.imprint","IMPRINT",EDGE,{"derivedFrom":sQuery(id+"F0.wireOp",EDGE,"E4.0.2.0")}),1.0]])]});
            var Q50;
            Q50=makeQuery(id+"F0.imprint","IMPRINT",FACE,{"disambiguationData":[TD([[makeQuery(id+"F0.imprint","IMPRINT",EDGE,{"derivedFrom":sQuery(id+"F0.wireOp",EDGE,"E3.0.3.0")}),1.0]])]});
            var Q51;
            Q51=makeQuery(id+"F0.imprint","IMPRINT",FACE,{"disambiguationData":[TD([[makeQuery(id+"F0.imprint","IMPRINT",EDGE,{"derivedFrom":sQuery(id+"F0.wireOp",EDGE,"E3.0.4.0")}),1.0]])]});
            extrude(context, id + "F1", {"entities" : qUnion([Q0, Q1, Q2, Q3, Q4, Q5, Q6, Q7, Q8, Q9, Q10, Q11, Q12, Q13, Q14, Q15, Q16, Q17, Q18, Q19, Q20, Q21, Q22, Q23, Q24, Q25, Q26, Q27, Q28, Q29, Q30, Q31, Q32, Q33, Q34, Q35, Q36, Q37, Q38, Q39, Q40, Q41, Q42, Q43, Q44, Q45, Q46, Q47, Q48, Q49, Q50, Q51]), "oppositeDirection" : true, "depth" : 1 * mm, "offsetDistance" : 25 * mm});
        }
    });
